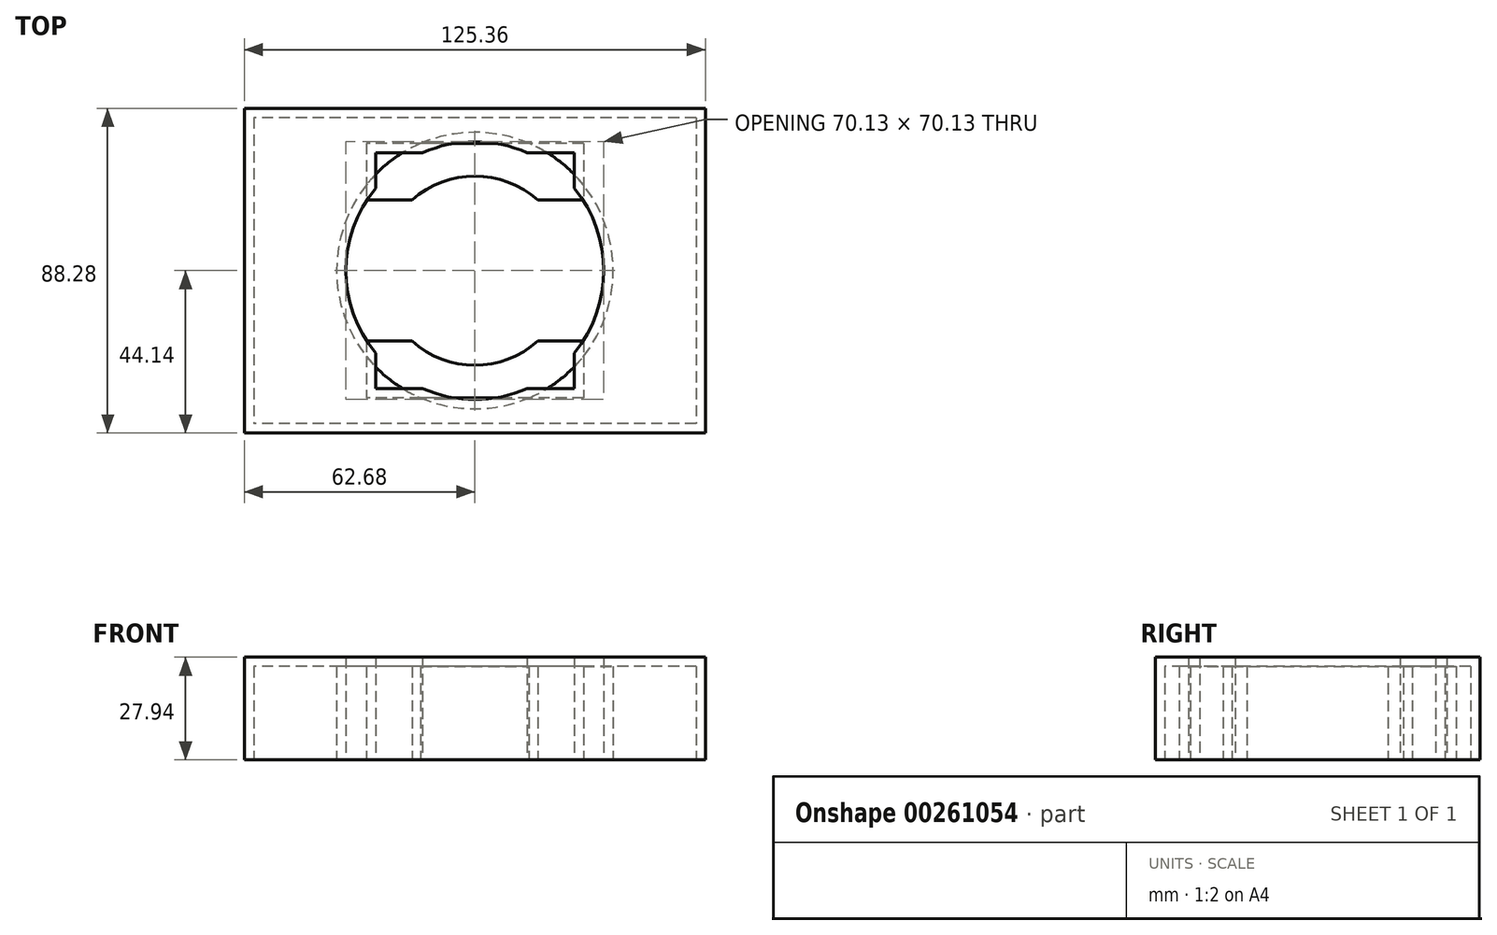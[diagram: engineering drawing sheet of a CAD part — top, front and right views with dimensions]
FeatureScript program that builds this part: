
annotation { "Feature Type Name" : "Feature", "Feature Type Description" : "" }
export const myFeature = defineFeature(function(context is Context, id is Id, definition is map)
    precondition{}
    {
        {
            var Q0;
            Q0=qCreatedBy(makeId("Top.planeOp"),FACE);
            var sketch = newSketch(context, id + "F0", { "sketchPlane" : qUnion([Q0])});
            skLineSegment(sketch, "E0.bottom", {"start": v(50.9, 34.6) * mm, "end": v(-50.9, 34.6) * mm});
            skLineSegment(sketch, "E0.top", {"start": v(50.9, -34.6) * mm, "end": v(-50.9, -34.6) * mm});
            skLineSegment(sketch, "E0.left", {"start": v(50.9, 34.6) * mm, "end": v(50.9, -34.6) * mm});
            skLineSegment(sketch, "E0.right", {"start": v(-50.9, 34.6) * mm, "end": v(-50.9, -34.6) * mm});
            skPoint(sketch, "E0.middle", {"position": v(0, 0) * mm});
            skLineSegment(sketch, "E1.bottom", {"start": v(60.14, 41.6) * mm, "end": v(-60.14, 41.6) * mm});
            skLineSegment(sketch, "E1.top", {"start": v(60.14, -41.6) * mm, "end": v(-60.14, -41.6) * mm});
            skLineSegment(sketch, "E1.left", {"start": v(60.14, 41.6) * mm, "end": v(60.14, -41.6) * mm});
            skLineSegment(sketch, "E1.right", {"start": v(-60.14, 41.6) * mm, "end": v(-60.14, -41.6) * mm});
            skLineSegment(sketch, "E2.bottom", {"start": v(29.54, 34.6) * mm, "end": v(-29.54, 34.6) * mm});
            skLineSegment(sketch, "E2.top", {"start": v(29.54, -34.6) * mm, "end": v(-29.54, -34.6) * mm});
            skLineSegment(sketch, "E2.left", {"start": v(29.54, 34.6) * mm, "end": v(29.54, -34.6) * mm});
            skLineSegment(sketch, "E2.right", {"start": v(-29.54, 34.6) * mm, "end": v(-29.54, -34.6) * mm});
            skCircle(sketch, "E3", {"center": v(0, 0) * mm, "radius": 37.6 * mm});
            skLineSegment(sketch, "E4.bottom", {"start": v(29.54, 19.18) * mm, "end": v(-29.54, 19.18) * mm});
            skLineSegment(sketch, "E4.top", {"start": v(29.54, -19.18) * mm, "end": v(-29.54, -19.18) * mm});
            skLineSegment(sketch, "E4.left", {"start": v(29.54, 19.18) * mm, "end": v(29.54, -19.18) * mm});
            skLineSegment(sketch, "E4.right", {"start": v(-29.54, 19.18) * mm, "end": v(-29.54, -19.18) * mm});
            skSolve(sketch);
        }
        {
            var Q0;
            Q0 = qSketchRegion(id + "F0", true);
            var Q1;
            {var subQ0=sQuery(id+"F0.wireOp",EDGE,"WBNERUox-NT9L-l1zi-AvUv-ES18iqVap7ck");Q1=makeQuery(id+"F0.imprint","IMPRINT",FACE,{"disambiguationData":[TD([[makeQuery(id+"F0.imprint","IMPRINT",EDGE,{"derivedFrom":subQ0}),1.0]])]});}
            var Q2;
            {var subQ5=sQuery(id+"F0.wireOp",EDGE,"E0.right");Q2=makeQuery(id+"F0.imprint","IMPRINT",FACE,{"disambiguationData":[TD([[makeQuery(id+"F0.imprint","IMPRINT",EDGE,{"derivedFrom":subQ5}),1.0]])]});}
            var Q3;
            {var subQ5=sQuery(id+"F0.wireOp",EDGE,"E0.left");Q3=makeQuery(id+"F0.imprint","IMPRINT",FACE,{"disambiguationData":[TD([[makeQuery(id+"F0.imprint","IMPRINT",EDGE,{"derivedFrom":subQ5}),-1.0]])]});}
            var Q4;
            {var subQ0=sQuery(id+"F0.wireOp",EDGE,"E2.top");Q4=makeQuery(id+"F0.imprint","IMPRINT",FACE,{"disambiguationData":[TD([[makeQuery(id+"F0.imprint","IMPRINT",EDGE,{"derivedFrom":subQ0}),-1.0]])]});}
            var Q5;
            {var subQ0=sQuery(id+"F0.wireOp",EDGE,"E2.bottom");Q5=makeQuery(id+"F0.imprint","IMPRINT",FACE,{"disambiguationData":[TD([[makeQuery(id+"F0.imprint","IMPRINT",EDGE,{"derivedFrom":subQ0}),1.0]])]});}
            var Q6;
            {var subQ0=sQuery(id+"F0.wireOp",EDGE,"E3");var subQ1=sQuery(id+"F0.wireOp",EDGE,"E2.right");var subQ2=makeQuery(id+"F0.imprint","INTERSECT",VERTEX,{"disambiguationData":[OD(0.0)],"derivedFrom":[subQ1,subQ0]});Q6=makeQuery(id+"F0.imprint","IMPRINT",FACE,{"disambiguationData":[TD([[makeQuery(id+"F0.imprint","IMPRINT",EDGE,{"disambiguationData":[TD([[subQ2,-1.0]])],"derivedFrom":subQ1}),-1.0]])]});}
            var Q7;
            {var subQ0=sQuery(id+"F0.wireOp",EDGE,"E3");var subQ1=sQuery(id+"F0.wireOp",EDGE,"E2.left");var subQ2=makeQuery(id+"F0.imprint","INTERSECT",VERTEX,{"disambiguationData":[OD(0.0)],"derivedFrom":[subQ1,subQ0]});Q7=makeQuery(id+"F0.imprint","IMPRINT",FACE,{"disambiguationData":[TD([[makeQuery(id+"F0.imprint","IMPRINT",EDGE,{"disambiguationData":[TD([[subQ2,-1.0]])],"derivedFrom":subQ1}),1.0]])]});}
            var Q8;
            {var subQ0=sQuery(id+"F0.wireOp",EDGE,"E4.top");Q8=makeQuery(id+"F0.imprint","IMPRINT",FACE,{"disambiguationData":[TD([[makeQuery(id+"F0.imprint","IMPRINT",EDGE,{"derivedFrom":subQ0}),1.0]])]});}
            var Q9;
            {var subQ0=sQuery(id+"F0.wireOp",EDGE,"E4.bottom");Q9=makeQuery(id+"F0.imprint","IMPRINT",FACE,{"disambiguationData":[TD([[makeQuery(id+"F0.imprint","IMPRINT",EDGE,{"derivedFrom":subQ0}),-1.0]])]});}
            extrude(context, id + "F1", {"entities" : qUnion([Q0, Q1, Q2, Q3, Q4, Q5, Q6, Q7, Q8, Q9]), "depth" : 25.4 * mm});
        }
        {
            var Q0;
            Q0=qCreatedBy(makeId("Top.planeOp"),FACE);
            var sketch = newSketch(context, id + "F2", { "sketchPlane" : qUnion([Q0])});
            skCircle(sketch, "E5", {"center": v(0, 0) * mm, "radius": 25.7 * mm});
            skSolve(sketch);
        }
        {
            var Q0;
            Q0 = qSketchRegion(id + "F2", true);
            extrude(context, id + "F3", {"entities" : qUnion([Q0]), "operationType" : NewBodyOperationType.REMOVE, "endBound" : BoundingType.SYMMETRIC, "depth" : 92.46 * mm});
        }
        {
            var Q0;
            Q0=makeQuery(id+"F1.opExtrude","CAP_FACE",FACE,{"disambiguationData":[OSD([sQuery(id+"F0.wireOp",EDGE,"E0.bottom"),sQuery(id+"F0.wireOp",EDGE,"E0.top"),sQuery(id+"F0.wireOp",EDGE,"E0.left"),sQuery(id+"F0.wireOp",EDGE,"E0.right"),sQuery(id+"F0.wireOp",EDGE,"E1.bottom"),sQuery(id+"F0.wireOp",EDGE,"E1.top"),sQuery(id+"F0.wireOp",EDGE,"E1.left"),sQuery(id+"F0.wireOp",EDGE,"E1.right"),sQuery(id+"F0.wireOp",EDGE,"WBNERUox-NT9L-l1zi-AvUv-ES18iqVap7ck"),sQuery(id+"F0.wireOp",EDGE,"a9caf0f8-7268-4247-a3bd-da9464e2ed75.trimOffspring")])],"isStart":true});
            shell(context, id + "F4", {"entities" : qUnion([Q0]), "thickness" : 2.54 * mm, "oppositeDirection" : true});
        }
    });
